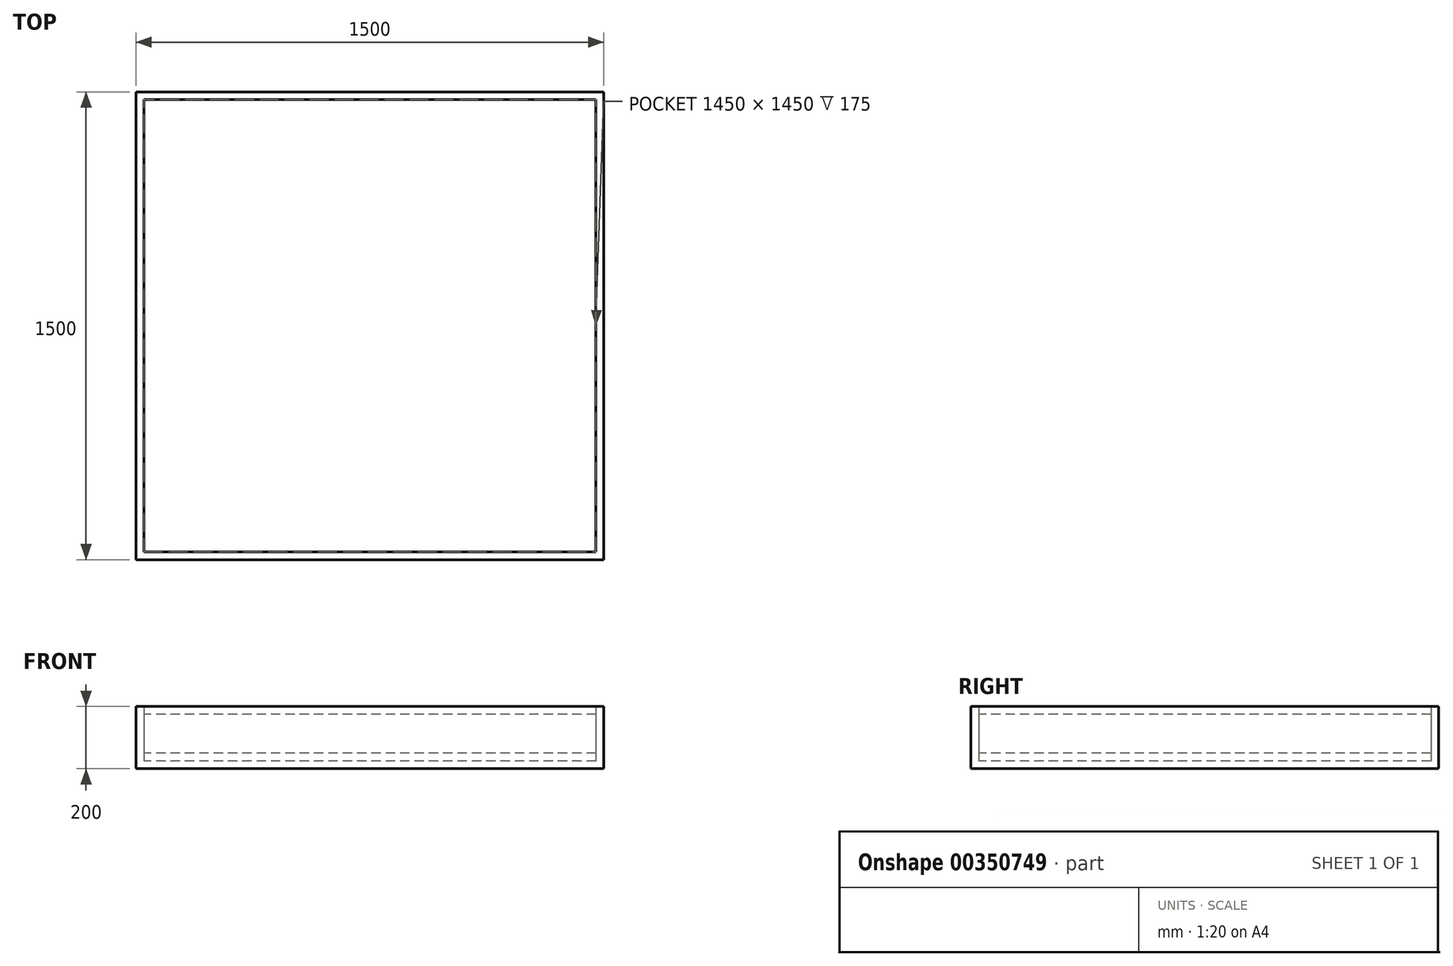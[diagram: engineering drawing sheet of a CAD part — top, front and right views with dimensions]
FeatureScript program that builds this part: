
annotation { "Feature Type Name" : "Feature", "Feature Type Description" : "" }
export const myFeature = defineFeature(function(context is Context, id is Id, definition is map)
    precondition{}
    {
        {
            var Q0;
            Q0=qCreatedBy(makeId("Top.planeOp"),FACE);
            var sketch = newSketch(context, id + "F0", { "sketchPlane" : qUnion([Q0])});
            skLineSegment(sketch, "E0.bottom", {"start": v(750, 750) * mm, "end": v(-750, 750) * mm});
            skLineSegment(sketch, "E0.top", {"start": v(750, -750) * mm, "end": v(-750, -750) * mm});
            skLineSegment(sketch, "E0.left", {"start": v(750, 750) * mm, "end": v(750, -750) * mm});
            skLineSegment(sketch, "E0.right", {"start": v(-750, 750) * mm, "end": v(-750, -750) * mm});
            skPoint(sketch, "E0.middle", {"position": v(0, 0) * mm});
            skSolve(sketch);
        }
        {
            var Q0;
            Q0=makeQuery(id+"F0.imprint","IMPRINT",FACE,{"disambiguationData":[TD([[makeQuery(id+"F0.imprint","IMPRINT",EDGE,{"derivedFrom":sQuery(id+"F0.wireOp",EDGE,"E0.bottom")}),1.0]])]});
            extrude(context, id + "F1", {"entities" : qUnion([Q0]), "depth" : 25 * mm});
        }
        {
            var Q0;
            Q0=makeQuery(id+"F1.opExtrude","CAP_FACE",FACE,{"disambiguationData":[OSD([sQuery(id+"F0.wireOp",EDGE,"E0.bottom"),sQuery(id+"F0.wireOp",EDGE,"E0.top"),sQuery(id+"F0.wireOp",EDGE,"E0.left"),sQuery(id+"F0.wireOp",EDGE,"E0.right")])],"isStart":false});
            var sketch = newSketch(context, id + "F2", { "sketchPlane" : qUnion([Q0])});
            skLineSegment(sketch, "E1.bottom", {"start": v(725, 725) * mm, "end": v(-725, 725) * mm});
            skLineSegment(sketch, "E1.top", {"start": v(725, -725) * mm, "end": v(-725, -725) * mm});
            skLineSegment(sketch, "E1.left", {"start": v(725, 725) * mm, "end": v(725, -725) * mm});
            skLineSegment(sketch, "E1.right", {"start": v(-725, 725) * mm, "end": v(-725, -725) * mm});
            skPoint(sketch, "E1.middle", {"position": v(0, 0) * mm});
            skSolve(sketch);
        }
        {
            var Q0;
            Q0=makeQuery(id+"F2.imprint","IMPRINT",FACE,{"disambiguationData":[TD([[makeQuery(id+"F2.imprint","IMPRINT",EDGE,{"derivedFrom":sQuery(id+"F2.wireOp",EDGE,"E1.bottom")}),-1.0]])]});
            extrude(context, id + "F3", {"entities" : qUnion([Q0]), "operationType" : NewBodyOperationType.ADD, "depth" : (200 - 25) * mm});
        }
        {
            var Q0;
            Q0=makeQuery(id+"F1.opExtrude","CAP_FACE",FACE,{"disambiguationData":[OSD([sQuery(id+"F0.wireOp",EDGE,"E0.bottom"),sQuery(id+"F0.wireOp",EDGE,"E0.top"),sQuery(id+"F0.wireOp",EDGE,"E0.left"),sQuery(id+"F0.wireOp",EDGE,"E0.right")])],"isStart":false});
            extrude(context, id + "F4", {"entities" : qUnion([Q0]), "depth" : 25 * mm});
        }
        {
            var Q0;
            Q0=makeQuery(id+"F4.opExtrude","CAP_FACE",FACE,{"disambiguationData":[OSD([sQuery(id+"F0.wireOp",EDGE,"E0.bottom"),sQuery(id+"F0.wireOp",EDGE,"E0.top"),sQuery(id+"F0.wireOp",EDGE,"E0.left"),sQuery(id+"F0.wireOp",EDGE,"E0.right")])],"isStart":false});
            var Q1;
            Q1=makeQuery(id+"F3.opExtrude","CAP_FACE",FACE,{"disambiguationData":[OSD([sQuery(id+"F0.wireOp",EDGE,"E0.bottom"),sQuery(id+"F0.wireOp",EDGE,"E0.top"),sQuery(id+"F0.wireOp",EDGE,"E0.left"),sQuery(id+"F0.wireOp",EDGE,"E0.right"),sQuery(id+"F2.wireOp",EDGE,"E1.bottom"),sQuery(id+"F2.wireOp",EDGE,"E1.top"),sQuery(id+"F2.wireOp",EDGE,"E1.left"),sQuery(id+"F2.wireOp",EDGE,"E1.right")])],"isStart":false});
            extrude(context, id + "F5", {"entities" : qUnion([Q0]), "endBoundEntityFace" : qUnion([Q1]), "depth" : (200 - 25 - 25 - 25) * mm});
        }
        {
            var Q0;
            Q0=makeQuery(id+"F5.opExtrude","CAP_FACE",FACE,{"disambiguationData":[OSD([sQuery(id+"F0.wireOp",EDGE,"E0.bottom"),sQuery(id+"F0.wireOp",EDGE,"E0.top"),sQuery(id+"F0.wireOp",EDGE,"E0.left"),sQuery(id+"F0.wireOp",EDGE,"E0.right")])],"isStart":false});
            extrude(context, id + "F6", {"entities" : qUnion([Q0]), "depth" : 25 * mm});
        }
    });
